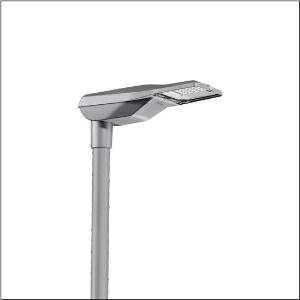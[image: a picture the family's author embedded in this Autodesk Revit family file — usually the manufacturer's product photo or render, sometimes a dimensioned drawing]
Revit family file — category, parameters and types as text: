
# Revit family: streetlight_sl_21_iq_micro___st0_8a_5xe1c21d08cb_82e6
name_source: partatom
category: Lighting Fixtures
units: mm (PartAtom-declared; Revit-internal decimal feet)

## family parameters
Cut with Voids When Loaded = No
Host = Face
Light Source = No
Part Type = Normal
Room Calculation Point = No
Round Connector Dimension = Use Diameter
Shared = No

## types (1)
- --- (1 x LED, 2380 lm, 19.4 W, 2200K)
    Apparent Load = 19 VA
    CIE Flux Codes = 38 75 97 100 100
    Color Rendering = 70
    Color Temperature = 2200K
    Default Elevation = 1800 mm
    Description = Streetlight SL 21 iQ micro, mast luminaire, primary light control with lens, of PMMA, primary optical cover: cover, of toughened safety glass, transparent, light distribution: ST0.8a, light emission: direct distribution, primary light characteristic: asymmetric, installation type: post-top, side-entry, LED, High Power LED, rated luminous flux: 2.380lm, luminous efficacy: 123lm/W, light colour: 722, colour temperature: 2200K, control: Auto-Match, Temp-Guard, Lumen-Switch, Night-Set, Smart-Wire, Light-Fading, Desk-Remote (wireless, voltage-free reading and setting of iQ features in the workshop via application-optimized NFC function/RFID function), optimised constant luminous flux control (CLO 2.0), pre-setting: linear dimming characteristic, mains connection: 220..240V, AC, 50/60Hz, start of lifetime: 19W, end of service life: 20W, reduction: 10W, luminaire housing, of diecast aluminium, powder-coated, Siteco® metallic grey (DB 702S), corrosivity category C5 mid according to DIN EN ISO 12944, please order mast flange separately, inclination adjustable: 0°, 5°, 10°, 15°, sealing non-destructively replaceable, multi-level sealing system, length: 528mm, width: 235mm, height: 110mm, mast flange for spigot size: 42mm (side-entry): 5XC10008XM4, 60/48mm (side-entry/post-top): 5XC10108XM2, 76/60mm (side-entry/post-top): 5XC10108XM1, protection rating (complete): IP66, insulation class (complete): insulation class II (safety insulation), certification: CE, ENEC, ENEC+, VDE, impact resistance: IK09, permissible operating ambient temperature for outdoor applications: -40..+50°C, standard-compliant lighting for roads and squares, packaging unit: 1 piece

Light Distribution: ST0.8a
    Height = 110 mm
    Lamp = 1 x LED
    Lamp Light Flux = 2380 lm
    Lamp Power = 19.4 W
    Lamp count = 1
    Length = 528 mm
    Luminous efficacy = 123 lm/W
    Manufacturer = Siteco
    ModVariant = No
    Model = 5XE1C21D08CB
    Number of Poles = 1
    OnlyDefault = Yes
    Power Factor = 1
    Product Name = Streetlight SL 21 iQ micro | ST0.8a
    Product group = mast luminaire | pylon top
    ProductGroupID = 6100
    Protection Class = Protection class II
    Protection Degree = IP 66
    RLX_Detail_Level = 1
    RLX_Emergency_Light_Flux = 0 lm
    RLX_Emergency_Type = 0
    RLX_Emergency_Type_DB = No
    RlxData = <blob elided: 98557 chars, md5=9fc16609>
    Socket = socket
    Standby Power = 0 W
    System Light Flux = 2380 lm
    System Power = 19 W
    Type Comments = factory setting: luminous flux: 100 % | dim-lin: 254 | 387 mA
    Type Image = l_1006881.jpg
    URL = http://relux.com
    VarID = @adj_108339
    Voltage = 0 V
    Weight = 0.00 kg
    Width = 235 mm

## geometry (parser evidence)
native form markers: Blend x4, Sweep x11
no freeform markers — native parametric forms only
